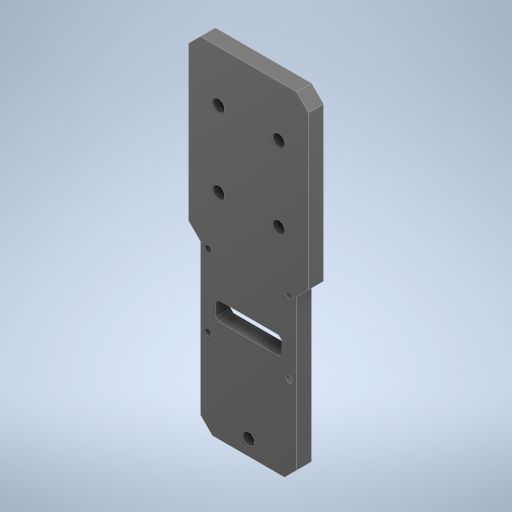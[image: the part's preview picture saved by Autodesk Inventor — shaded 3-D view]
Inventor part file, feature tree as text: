
AUTODESK INVENTOR PART (.ipt)
format: ipt  version: 2024.2 (Build 282272000, 272)  size: 256,000 bytes
history: native  units: in
note: dims shown in document units (in); Inventor stores cm internally (conversion verified against a paired STEP export)
features: extrude x1, chamfer x1, sketch x1, other x1
ambient origin geometry x8: Origin, YZ Plane, XZ Plane, XY Plane, X Axis, Y Axis, Z Axis, Center Point
bodies: Solid1 (feature_tree)
feature tree (4):
  extrude  "Extrusion1"  Depth=0.0787in
  chamfer  "Chamfer1"  Distance=0.2441in
  sketch  "Sketch1"  dims[d0=1.3307in d1=0.4331in d2=0.2441in d3=0.8661in d4=0.3937in d5=0.0in d6=0.0394in d7=0.0787in d8=45.0deg]
  other  "Cortar-Extruir9"
